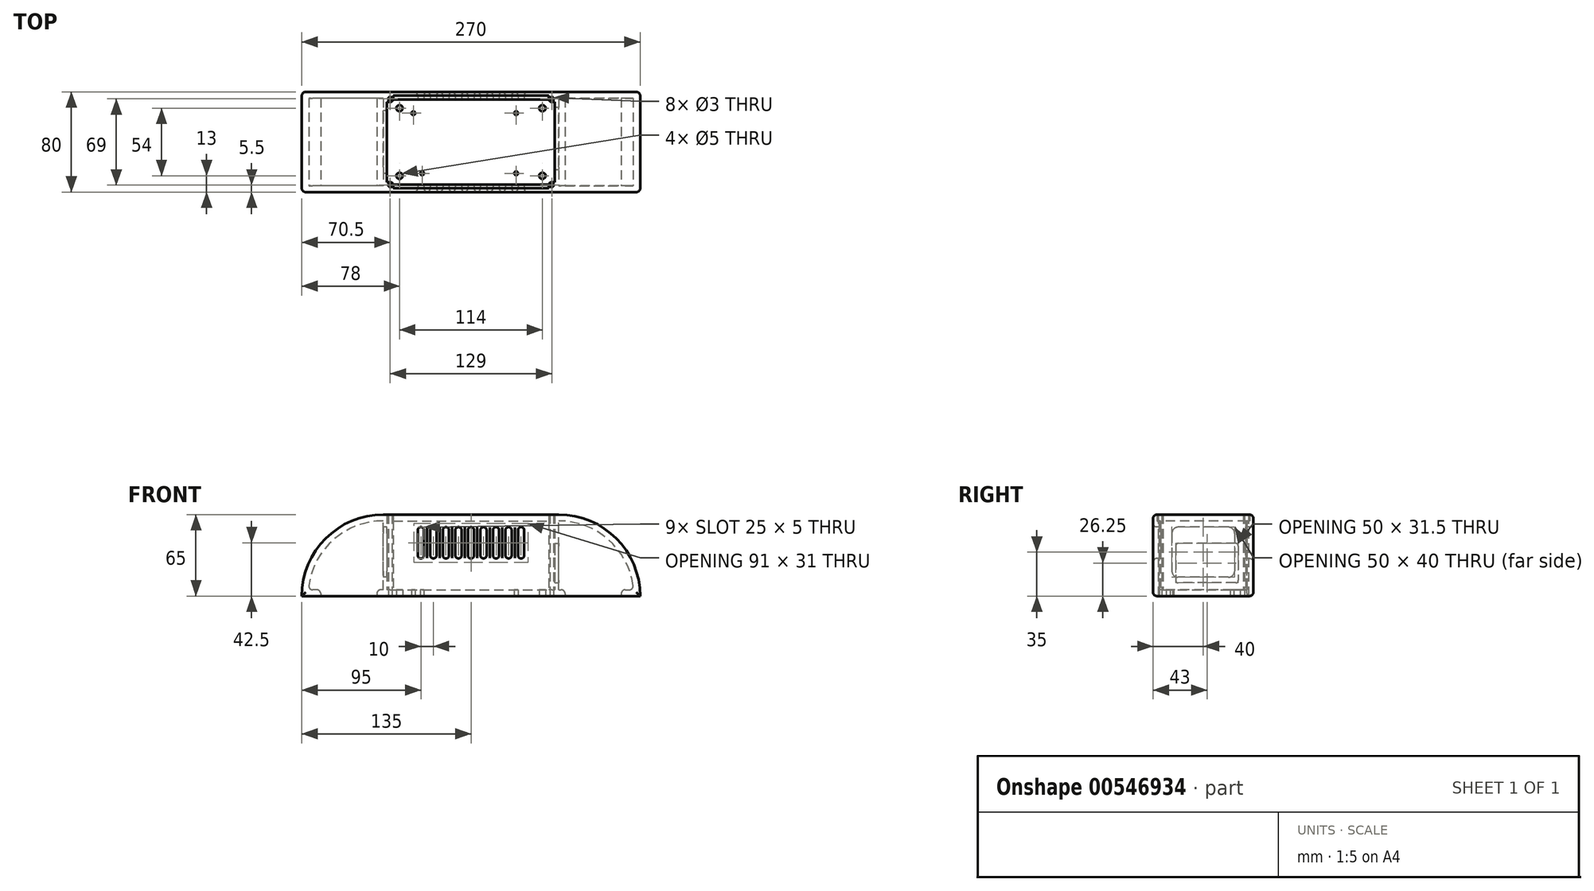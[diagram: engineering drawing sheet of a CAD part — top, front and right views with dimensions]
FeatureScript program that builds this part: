
annotation { "Feature Type Name" : "Feature", "Feature Type Description" : "" }
export const myFeature = defineFeature(function(context is Context, id is Id, definition is map)
    precondition{}
    {
        {
            var Q0;
            Q0=qCreatedBy(makeId("Top.planeOp"),FACE);
            var sketch = newSketch(context, id + "F0", { "sketchPlane" : qUnion([Q0])});
            skLineSegment(sketch, "E0", {"start": v(0, 0) * mm, "end": v(140, 0) * mm});
            skLineSegment(sketch, "E1", {"start": v(140, 0) * mm, "end": v(140, 80) * mm});
            skLineSegment(sketch, "E2", {"start": v(140, 80) * mm, "end": v(0, 80) * mm});
            skLineSegment(sketch, "E3", {"start": v(0, 80) * mm, "end": v(0, 0) * mm});
            skLineSegment(sketch, "E4.0", {"start": v(3, 72) * mm, "end": v(3, 8) * mm});
            skLineSegment(sketch, "E5.0", {"start": v(8, 3) * mm, "end": v(132, 3) * mm});
            skLineSegment(sketch, "E6.0", {"start": v(137, 8) * mm, "end": v(137, 72) * mm});
            skLineSegment(sketch, "E7.0", {"start": v(0, 40) * mm, "end": v(140, 40) * mm, "construction": true});
            skLineSegment(sketch, "E8.0", {"start": v(70, 80) * mm, "end": v(70, 0) * mm, "construction": true});
            skLineSegment(sketch, "E9.0", {"start": v(19, 66) * mm, "end": v(19, 13) * mm, "construction": true});
            skLineSegment(sketch, "E10.0", {"start": v(121, 66) * mm, "end": v(121, 13) * mm, "construction": true});
            skLineSegment(sketch, "E11.0", {"start": v(19, 66) * mm, "end": v(121, 66) * mm, "construction": true});
            skLineSegment(sketch, "E12.0", {"start": v(19, 13) * mm, "end": v(121, 13) * mm, "construction": true});
            skLineSegment(sketch, "E13.0", {"start": v(24, 66) * mm, "end": v(24, 63) * mm, "construction": true});
            skLineSegment(sketch, "E14.0", {"start": v(24, 63) * mm, "end": v(106, 63) * mm, "construction": true});
            skLineSegment(sketch, "E15.0", {"start": v(31, 15) * mm, "end": v(31, 13) * mm, "construction": true});
            skLineSegment(sketch, "E16.0", {"start": v(106, 66) * mm, "end": v(106, 63) * mm, "construction": true});
            skLineSegment(sketch, "E17.0", {"start": v(31, 15) * mm, "end": v(106, 15) * mm, "construction": true});
            skLineSegment(sketch, "E18.trimOffspring", {"start": v(106, 15) * mm, "end": v(106, 13) * mm, "construction": true});
            skCircle(sketch, "E19", {"center": v(24, 63) * mm, "radius": 1.5 * mm});
            skCircle(sketch, "E20", {"center": v(106, 63) * mm, "radius": 1.5 * mm});
            skCircle(sketch, "E21", {"center": v(31, 15) * mm, "radius": 1.5 * mm});
            skCircle(sketch, "E22", {"center": v(106, 15) * mm, "radius": 1.5 * mm});
            skLineSegment(sketch, "E23.0", {"start": v(5.5, 77) * mm, "end": v(5.5, 74.5) * mm, "construction": true});
            skLineSegment(sketch, "E24.0", {"start": v(134.5, 3) * mm, "end": v(134.5, 5.5) * mm, "construction": true});
            skLineSegment(sketch, "E25.0", {"start": v(3, 5.5) * mm, "end": v(5.5, 5.5) * mm, "construction": true});
            skLineSegment(sketch, "E26.0", {"start": v(137, 74.5) * mm, "end": v(134.5, 74.5) * mm, "construction": true});
            skLineSegment(sketch, "E27.trimOffspring", {"start": v(5.5, 74.5) * mm, "end": v(3, 74.5) * mm, "construction": true});
            skLineSegment(sketch, "E28.trimOffspring", {"start": v(134.5, 74.5) * mm, "end": v(134.5, 77) * mm, "construction": true});
            skLineSegment(sketch, "E29.trimOffspring", {"start": v(134.5, 5.5) * mm, "end": v(137, 5.5) * mm, "construction": true});
            skLineSegment(sketch, "E30.trimOffspring", {"start": v(5.5, 5.5) * mm, "end": v(5.5, 3) * mm, "construction": true});
            skLineSegment(sketch, "E31.0", {"start": v(8, 77) * mm, "end": v(8, 74.5) * mm});
            skLineSegment(sketch, "E32.0", {"start": v(132, 3) * mm, "end": v(132, 5.5) * mm});
            skLineSegment(sketch, "E33.0", {"start": v(137, 72) * mm, "end": v(134.5, 72) * mm});
            skLineSegment(sketch, "E34.0", {"start": v(3, 8) * mm, "end": v(5.5, 8) * mm});
            skLineSegment(sketch, "E35.trimOffspring", {"start": v(8, 5.5) * mm, "end": v(8, 3) * mm});
            skLineSegment(sketch, "E36.trimOffspring", {"start": v(5.5, 72) * mm, "end": v(3, 72) * mm});
            skLineSegment(sketch, "E37.trimOffspring", {"start": v(132, 74.5) * mm, "end": v(132, 77) * mm});
            skLineSegment(sketch, "E38.trimOffspring", {"start": v(134.5, 8) * mm, "end": v(137, 8) * mm});
            skPoint(sketch, "E39.visualSharp", {"position": v(8, 72) * mm});
            skArc(sketch, "E39.filletArc", {"start": v(5.5, 72) * mm, "mid": v(7.27, 72.73) * mm, "end": v(8, 74.5) * mm});
            skPoint(sketch, "E40.visualSharp", {"position": v(132, 72) * mm});
            skArc(sketch, "E40.filletArc", {"start": v(132, 74.5) * mm, "mid": v(132.73, 72.73) * mm, "end": v(134.5, 72) * mm});
            skPoint(sketch, "E41.visualSharp", {"position": v(132, 8) * mm});
            skArc(sketch, "E41.filletArc", {"start": v(134.5, 8) * mm, "mid": v(132.73, 7.27) * mm, "end": v(132, 5.5) * mm});
            skPoint(sketch, "E42.visualSharp", {"position": v(8, 8) * mm});
            skArc(sketch, "E42.filletArc", {"start": v(8, 5.5) * mm, "mid": v(7.27, 7.27) * mm, "end": v(5.5, 8) * mm});
            skCircle(sketch, "E43", {"center": v(5.5, 74.5) * mm, "radius": 1.5 * mm});
            skLineSegment(sketch, "E44.trimOffspring", {"start": v(132, 77) * mm, "end": v(8, 77) * mm});
            skCircle(sketch, "E45", {"center": v(134.5, 74.5) * mm, "radius": 1.5 * mm});
            skCircle(sketch, "E46", {"center": v(134.5, 5.5) * mm, "radius": 1.5 * mm});
            skCircle(sketch, "E47", {"center": v(5.5, 5.5) * mm, "radius": 1.5 * mm});
            skLineSegment(sketch, "E48.0", {"start": v(13, 72) * mm, "end": v(13, 8) * mm, "construction": true});
            skLineSegment(sketch, "E49.0", {"start": v(132, 67) * mm, "end": v(127, 67) * mm, "construction": true});
            skLineSegment(sketch, "E50.0", {"start": v(127, 8) * mm, "end": v(127, 72) * mm, "construction": true});
            skLineSegment(sketch, "E51.0", {"start": v(13, 13) * mm, "end": v(127, 13) * mm, "construction": true});
            skLineSegment(sketch, "E52.trimOffspring", {"start": v(13, 67) * mm, "end": v(8, 67) * mm, "construction": true});
            skCircle(sketch, "E53", {"center": v(13, 67) * mm, "radius": 2.5 * mm});
            skCircle(sketch, "E54", {"center": v(127, 67) * mm, "radius": 2.5 * mm});
            skCircle(sketch, "E55", {"center": v(127, 13) * mm, "radius": 2.5 * mm});
            skCircle(sketch, "E56", {"center": v(13, 13) * mm, "radius": 2.5 * mm});
            skLineSegment(sketch, "E57.0", {"start": v(7.95, 6) * mm, "end": v(132.05, 6) * mm});
            skLineSegment(sketch, "E58.0", {"start": v(132.05, 74) * mm, "end": v(7.95, 74) * mm});
            skSolve(sketch);
        }
        {
            var Q0;
            Q0=makeQuery(id+"F0.imprint","IMPRINT",FACE,{"disambiguationData":[TD([[makeQuery(id+"F0.imprint","IMPRINT",EDGE,{"derivedFrom":sQuery(id+"F0.wireOp",EDGE,"E4.0")}),1.0]])]});
            extrude(context, id + "F1", {"entities" : qUnion([Q0]), "depth" : 5 * mm, "offsetDistance" : 25 * mm});
        }
        {
            var Q0;
            Q0=makeQuery(id+"F0.imprint","IMPRINT",FACE,{"disambiguationData":[TD([[makeQuery(id+"F0.imprint","IMPRINT",EDGE,{"derivedFrom":sQuery(id+"F0.wireOp",EDGE,"E0")}),1.0]])]});
            extrude(context, id + "F2", {"entities" : qUnion([Q0]), "operationType" : NewBodyOperationType.ADD, "depth" : 65 * mm, "offsetDistance" : 25 * mm});
        }
        {
            var Q0;
            Q0=qCreatedBy(makeId("Front.planeOp"),FACE);
            var sketch = newSketch(context, id + "F3", { "sketchPlane" : qUnion([Q0])});
            skLineSegment(sketch, "E59", {"start": v(0, 0) * mm, "end": v(0, 30) * mm, "construction": true});
            skLineSegment(sketch, "E60", {"start": v(30, 30) * mm, "end": v(30, 30) * mm});
            skLineSegment(sketch, "E61", {"start": v(0, 30) * mm, "end": v(0, 55) * mm, "construction": true});
            skLineSegment(sketch, "E62", {"start": v(30, 55) * mm, "end": v(30, 55) * mm});
            skLineSegment(sketch, "E63.0", {"start": v(30, 30) * mm, "end": v(30, 55) * mm, "construction": true});
            skLineSegment(sketch, "E64.0", {"start": v(40, 30) * mm, "end": v(40, 55) * mm, "construction": true});
            skLineSegment(sketch, "E65.0", {"start": v(50, 30) * mm, "end": v(50, 55) * mm, "construction": true});
            skLineSegment(sketch, "E66.0", {"start": v(60, 30) * mm, "end": v(60, 55) * mm, "construction": true});
            skLineSegment(sketch, "E67.0", {"start": v(70, 30) * mm, "end": v(70, 55) * mm, "construction": true});
            skLineSegment(sketch, "E68.0", {"start": v(80, 30) * mm, "end": v(80, 55) * mm, "construction": true});
            skLineSegment(sketch, "E69.0", {"start": v(90, 30) * mm, "end": v(90, 55) * mm, "construction": true});
            skLineSegment(sketch, "E70.0", {"start": v(100, 30) * mm, "end": v(100, 55) * mm, "construction": true});
            skLineSegment(sketch, "E71.0", {"start": v(110, 30) * mm, "end": v(110, 55) * mm, "construction": true});
            skLineSegment(sketch, "E72.0", {"start": v(32.5, 32.5) * mm, "end": v(32.5, 52.5) * mm});
            skLineSegment(sketch, "E73.0", {"start": v(27.5, 32.5) * mm, "end": v(27.5, 52.5) * mm});
            skLineSegment(sketch, "E74.MirrorCS", {"start": v(47.5, 32.5) * mm, "end": v(47.5, 52.5) * mm});
            skLineSegment(sketch, "E75.MirrorCS", {"start": v(52.5, 32.5) * mm, "end": v(52.5, 52.5) * mm});
            skLineSegment(sketch, "E76.MirrorCS", {"start": v(67.5, 32.5) * mm, "end": v(67.5, 52.5) * mm});
            skLineSegment(sketch, "E77.MirrorCS", {"start": v(72.5, 32.5) * mm, "end": v(72.5, 52.5) * mm});
            skLineSegment(sketch, "E78.MirrorCS", {"start": v(87.5, 32.5) * mm, "end": v(87.5, 52.5) * mm});
            skLineSegment(sketch, "E79.MirrorCS", {"start": v(92.5, 32.5) * mm, "end": v(92.5, 52.5) * mm});
            skLineSegment(sketch, "E80.MirrorCS", {"start": v(107.5, 32.5) * mm, "end": v(107.5, 52.5) * mm});
            skLineSegment(sketch, "E81.MirrorCS", {"start": v(112.5, 32.5) * mm, "end": v(112.5, 52.5) * mm});
            skLineSegment(sketch, "E82.0", {"start": v(42.5, 32.5) * mm, "end": v(42.5, 52.5) * mm});
            skLineSegment(sketch, "E83.0", {"start": v(37.5, 32.5) * mm, "end": v(37.5, 52.5) * mm});
            skLineSegment(sketch, "E84.MirrorCS", {"start": v(57.5, 32.5) * mm, "end": v(57.5, 52.5) * mm});
            skLineSegment(sketch, "E85.MirrorCS", {"start": v(62.5, 32.5) * mm, "end": v(62.5, 52.5) * mm});
            skLineSegment(sketch, "E86.MirrorCS", {"start": v(77.5, 32.5) * mm, "end": v(77.5, 52.5) * mm});
            skLineSegment(sketch, "E87.MirrorCS", {"start": v(82.5, 32.5) * mm, "end": v(82.5, 52.5) * mm});
            skLineSegment(sketch, "E88.MirrorCS", {"start": v(97.5, 32.5) * mm, "end": v(97.5, 52.5) * mm});
            skLineSegment(sketch, "E89.MirrorCS", {"start": v(102.5, 32.5) * mm, "end": v(102.5, 52.5) * mm});
            skLineSegment(sketch, "E90.trimOffspring", {"start": v(110, 55) * mm, "end": v(110, 55) * mm});
            skLineSegment(sketch, "E91.trimOffspring", {"start": v(100, 55) * mm, "end": v(100, 55) * mm});
            skLineSegment(sketch, "E92.trimOffspring", {"start": v(90, 55) * mm, "end": v(90, 55) * mm});
            skLineSegment(sketch, "E93.trimOffspring", {"start": v(80, 55) * mm, "end": v(80, 55) * mm});
            skLineSegment(sketch, "E94.trimOffspring", {"start": v(70, 55) * mm, "end": v(70, 55) * mm});
            skLineSegment(sketch, "E95.trimOffspring", {"start": v(60, 55) * mm, "end": v(60, 55) * mm});
            skLineSegment(sketch, "E96.trimOffspring", {"start": v(50, 55) * mm, "end": v(50, 55) * mm});
            skLineSegment(sketch, "E97.trimOffspring", {"start": v(40, 55) * mm, "end": v(40, 55) * mm});
            skLineSegment(sketch, "E98.trimOffspring", {"start": v(40, 30) * mm, "end": v(40, 30) * mm});
            skLineSegment(sketch, "E99.trimOffspring", {"start": v(50, 30) * mm, "end": v(50, 30) * mm});
            skLineSegment(sketch, "E100.trimOffspring", {"start": v(60, 30) * mm, "end": v(60, 30) * mm});
            skLineSegment(sketch, "E101.trimOffspring", {"start": v(70, 30) * mm, "end": v(70, 30) * mm});
            skLineSegment(sketch, "E102.trimOffspring", {"start": v(80, 30) * mm, "end": v(80, 30) * mm});
            skLineSegment(sketch, "E103.trimOffspring", {"start": v(90, 30) * mm, "end": v(90, 30) * mm});
            skLineSegment(sketch, "E104.trimOffspring", {"start": v(100, 30) * mm, "end": v(100, 30) * mm});
            skLineSegment(sketch, "E105.trimOffspring", {"start": v(110, 30) * mm, "end": v(110, 30) * mm});
            skPoint(sketch, "E106.visualSharp", {"position": v(27.5, 55) * mm});
            skArc(sketch, "E106.filletArc", {"start": v(30, 55) * mm, "mid": v(28.23, 54.27) * mm, "end": v(27.5, 52.5) * mm});
            skPoint(sketch, "E107.visualSharp", {"position": v(32.5, 55) * mm});
            skArc(sketch, "E107.filletArc", {"start": v(32.5, 52.5) * mm, "mid": v(31.77, 54.27) * mm, "end": v(30, 55) * mm});
            skPoint(sketch, "E108.visualSharp", {"position": v(27.5, 30) * mm});
            skArc(sketch, "E108.filletArc", {"start": v(27.5, 32.5) * mm, "mid": v(28.23, 30.73) * mm, "end": v(30, 30) * mm});
            skPoint(sketch, "E109.visualSharp", {"position": v(32.5, 30) * mm});
            skArc(sketch, "E109.filletArc", {"start": v(30, 30) * mm, "mid": v(31.77, 30.73) * mm, "end": v(32.5, 32.5) * mm});
            skPoint(sketch, "E110.visualSharp", {"position": v(37.5, 30) * mm});
            skArc(sketch, "E110.filletArc", {"start": v(37.5, 32.5) * mm, "mid": v(38.23, 30.73) * mm, "end": v(40, 30) * mm});
            skPoint(sketch, "E111.visualSharp", {"position": v(42.5, 30) * mm});
            skArc(sketch, "E111.filletArc", {"start": v(40, 30) * mm, "mid": v(41.77, 30.73) * mm, "end": v(42.5, 32.5) * mm});
            skPoint(sketch, "E112.visualSharp", {"position": v(37.5, 55) * mm});
            skArc(sketch, "E112.filletArc", {"start": v(40, 55) * mm, "mid": v(38.23, 54.27) * mm, "end": v(37.5, 52.5) * mm});
            skPoint(sketch, "E113.visualSharp", {"position": v(42.5, 55) * mm});
            skArc(sketch, "E113.filletArc", {"start": v(42.5, 52.5) * mm, "mid": v(41.77, 54.27) * mm, "end": v(40, 55) * mm});
            skPoint(sketch, "E114.visualSharp", {"position": v(47.5, 55) * mm});
            skArc(sketch, "E114.filletArc", {"start": v(50, 55) * mm, "mid": v(48.23, 54.27) * mm, "end": v(47.5, 52.5) * mm});
            skPoint(sketch, "E115.visualSharp", {"position": v(52.5, 55) * mm});
            skArc(sketch, "E115.filletArc", {"start": v(52.5, 52.5) * mm, "mid": v(51.77, 54.27) * mm, "end": v(50, 55) * mm});
            skPoint(sketch, "E116.visualSharp", {"position": v(47.5, 30) * mm});
            skArc(sketch, "E116.filletArc", {"start": v(47.5, 32.5) * mm, "mid": v(48.23, 30.73) * mm, "end": v(50, 30) * mm});
            skPoint(sketch, "E117.visualSharp", {"position": v(52.5, 30) * mm});
            skArc(sketch, "E117.filletArc", {"start": v(50, 30) * mm, "mid": v(51.77, 30.73) * mm, "end": v(52.5, 32.5) * mm});
            skPoint(sketch, "E118.visualSharp", {"position": v(57.5, 55) * mm});
            skArc(sketch, "E118.filletArc", {"start": v(60, 55) * mm, "mid": v(58.23, 54.27) * mm, "end": v(57.5, 52.5) * mm});
            skPoint(sketch, "E119.visualSharp", {"position": v(62.5, 55) * mm});
            skArc(sketch, "E119.filletArc", {"start": v(62.5, 52.5) * mm, "mid": v(61.77, 54.27) * mm, "end": v(60, 55) * mm});
            skPoint(sketch, "E120.visualSharp", {"position": v(57.5, 30) * mm});
            skArc(sketch, "E120.filletArc", {"start": v(57.5, 32.5) * mm, "mid": v(58.23, 30.73) * mm, "end": v(60, 30) * mm});
            skPoint(sketch, "E121.visualSharp", {"position": v(62.5, 30) * mm});
            skArc(sketch, "E121.filletArc", {"start": v(60, 30) * mm, "mid": v(61.77, 30.73) * mm, "end": v(62.5, 32.5) * mm});
            skPoint(sketch, "E122.visualSharp", {"position": v(67.5, 55) * mm});
            skArc(sketch, "E122.filletArc", {"start": v(70, 55) * mm, "mid": v(68.23, 54.27) * mm, "end": v(67.5, 52.5) * mm});
            skPoint(sketch, "E123.visualSharp", {"position": v(72.5, 55) * mm});
            skArc(sketch, "E123.filletArc", {"start": v(72.5, 52.5) * mm, "mid": v(71.77, 54.27) * mm, "end": v(70, 55) * mm});
            skPoint(sketch, "E124.visualSharp", {"position": v(67.5, 30) * mm});
            skArc(sketch, "E124.filletArc", {"start": v(67.5, 32.5) * mm, "mid": v(68.23, 30.73) * mm, "end": v(70, 30) * mm});
            skPoint(sketch, "E125.visualSharp", {"position": v(72.5, 30) * mm});
            skArc(sketch, "E125.filletArc", {"start": v(70, 30) * mm, "mid": v(71.77, 30.73) * mm, "end": v(72.5, 32.5) * mm});
            skPoint(sketch, "E126.visualSharp", {"position": v(77.5, 55) * mm});
            skArc(sketch, "E126.filletArc", {"start": v(80, 55) * mm, "mid": v(78.23, 54.27) * mm, "end": v(77.5, 52.5) * mm});
            skPoint(sketch, "E127.visualSharp", {"position": v(82.5, 55) * mm});
            skArc(sketch, "E127.filletArc", {"start": v(82.5, 52.5) * mm, "mid": v(81.77, 54.27) * mm, "end": v(80, 55) * mm});
            skPoint(sketch, "E128.visualSharp", {"position": v(77.5, 30) * mm});
            skArc(sketch, "E128.filletArc", {"start": v(77.5, 32.5) * mm, "mid": v(78.23, 30.73) * mm, "end": v(80, 30) * mm});
            skPoint(sketch, "E129.visualSharp", {"position": v(82.5, 30) * mm});
            skArc(sketch, "E129.filletArc", {"start": v(80, 30) * mm, "mid": v(81.77, 30.73) * mm, "end": v(82.5, 32.5) * mm});
            skPoint(sketch, "E130.visualSharp", {"position": v(87.5, 55) * mm});
            skArc(sketch, "E130.filletArc", {"start": v(90, 55) * mm, "mid": v(88.23, 54.27) * mm, "end": v(87.5, 52.5) * mm});
            skPoint(sketch, "E131.visualSharp", {"position": v(92.5, 55) * mm});
            skArc(sketch, "E131.filletArc", {"start": v(92.5, 52.5) * mm, "mid": v(91.77, 54.27) * mm, "end": v(90, 55) * mm});
            skPoint(sketch, "E132.visualSharp", {"position": v(87.5, 30) * mm});
            skArc(sketch, "E132.filletArc", {"start": v(87.5, 32.5) * mm, "mid": v(88.23, 30.73) * mm, "end": v(90, 30) * mm});
            skPoint(sketch, "E133.visualSharp", {"position": v(92.5, 30) * mm});
            skArc(sketch, "E133.filletArc", {"start": v(90, 30) * mm, "mid": v(91.77, 30.73) * mm, "end": v(92.5, 32.5) * mm});
            skPoint(sketch, "E134.visualSharp", {"position": v(97.5, 55) * mm});
            skArc(sketch, "E134.filletArc", {"start": v(100, 55) * mm, "mid": v(98.23, 54.27) * mm, "end": v(97.5, 52.5) * mm});
            skPoint(sketch, "E135.visualSharp", {"position": v(102.5, 55) * mm});
            skArc(sketch, "E135.filletArc", {"start": v(102.5, 52.5) * mm, "mid": v(101.77, 54.27) * mm, "end": v(100, 55) * mm});
            skPoint(sketch, "E136.visualSharp", {"position": v(97.5, 30) * mm});
            skArc(sketch, "E136.filletArc", {"start": v(97.5, 32.5) * mm, "mid": v(98.23, 30.73) * mm, "end": v(100, 30) * mm});
            skPoint(sketch, "E137.visualSharp", {"position": v(102.5, 30) * mm});
            skArc(sketch, "E137.filletArc", {"start": v(100, 30) * mm, "mid": v(101.77, 30.73) * mm, "end": v(102.5, 32.5) * mm});
            skPoint(sketch, "E138.visualSharp", {"position": v(107.5, 55) * mm});
            skArc(sketch, "E138.filletArc", {"start": v(110, 55) * mm, "mid": v(108.23, 54.27) * mm, "end": v(107.5, 52.5) * mm});
            skPoint(sketch, "E139.visualSharp", {"position": v(112.5, 55) * mm});
            skArc(sketch, "E139.filletArc", {"start": v(112.5, 52.5) * mm, "mid": v(111.77, 54.27) * mm, "end": v(110, 55) * mm});
            skPoint(sketch, "E140.visualSharp", {"position": v(107.5, 30) * mm});
            skArc(sketch, "E140.filletArc", {"start": v(107.5, 32.5) * mm, "mid": v(108.23, 30.73) * mm, "end": v(110, 30) * mm});
            skPoint(sketch, "E141.visualSharp", {"position": v(112.5, 30) * mm});
            skArc(sketch, "E141.filletArc", {"start": v(110, 30) * mm, "mid": v(111.77, 30.73) * mm, "end": v(112.5, 32.5) * mm});
            skArc(sketch, "E142", {"start": v(0, 65) * mm, "mid": v(-45.96, 45.96) * mm, "end": v(-65, 0) * mm});
            skLineSegment(sketch, "E143", {"start": v(0, 0) * mm, "end": v(0, 65) * mm});
            skLineSegment(sketch, "E144", {"start": v(0, 0) * mm, "end": v(-65, 0) * mm});
            skLineSegment(sketch, "E145", {"start": v(0, 0) * mm, "end": v(140, 0) * mm, "construction": true});
            skLineSegment(sketch, "E146", {"start": v(140, 0) * mm, "end": v(140, 65) * mm});
            skLineSegment(sketch, "E147", {"start": v(140, 0) * mm, "end": v(205, 0) * mm});
            skArc(sketch, "E148", {"start": v(205, 0) * mm, "mid": v(185.96, 45.96) * mm, "end": v(140, 65) * mm});
            skSolve(sketch);
        }
        {
            var Q0;
            Q0=qCreatedBy(makeId("Right.planeOp"),FACE);
            var sketch = newSketch(context, id + "F4", { "sketchPlane" : qUnion([Q0])});
            skLineSegment(sketch, "E149", {"start": v(0, 0) * mm, "end": v(0, 55) * mm, "construction": true});
            skLineSegment(sketch, "E150", {"start": v(20, 55) * mm, "end": v(60, 55) * mm});
            skLineSegment(sketch, "E151.0", {"start": v(40, 0) * mm, "end": v(40, 55) * mm, "construction": true});
            skLineSegment(sketch, "E152.0", {"start": v(35, 45) * mm, "end": v(35, 55) * mm, "construction": true});
            skLineSegment(sketch, "E153.0", {"start": v(65, 20) * mm, "end": v(65, 50) * mm});
            skLineSegment(sketch, "E154.0", {"start": v(15, 20) * mm, "end": v(15, 50) * mm});
            skLineSegment(sketch, "E155.0", {"start": v(20, 15) * mm, "end": v(60, 15) * mm});
            skPoint(sketch, "E156.visualSharp", {"position": v(65, 55) * mm});
            skArc(sketch, "E156.filletArc", {"start": v(65, 50) * mm, "mid": v(63.54, 53.54) * mm, "end": v(60, 55) * mm});
            skPoint(sketch, "E157.visualSharp", {"position": v(15, 55) * mm});
            skArc(sketch, "E157.filletArc", {"start": v(20, 55) * mm, "mid": v(16.46, 53.54) * mm, "end": v(15, 50) * mm});
            skPoint(sketch, "E158.visualSharp", {"position": v(15, 15) * mm});
            skArc(sketch, "E158.filletArc", {"start": v(15, 20) * mm, "mid": v(16.46, 16.46) * mm, "end": v(20, 15) * mm});
            skPoint(sketch, "E159.visualSharp", {"position": v(65, 15) * mm});
            skArc(sketch, "E159.filletArc", {"start": v(60, 15) * mm, "mid": v(63.54, 16.46) * mm, "end": v(65, 20) * mm});
            skSolve(sketch);
        }
        {
            var Q0;
            Q0=makeQuery(id+"F4.imprint","IMPRINT",FACE,{"disambiguationData":[TD([[makeQuery(id+"F4.imprint","IMPRINT",EDGE,{"derivedFrom":sQuery(id+"F4.wireOp",EDGE,"E150")}),-1.0]])]});
            extrude(context, id + "F5", {"entities" : qUnion([Q0]), "operationType" : NewBodyOperationType.REMOVE, "depth" : 10 * mm, "offsetDistance" : 25 * mm});
        }
        {
            var Q0;
            Q0=qCreatedBy(makeId("Right.planeOp"),FACE);
            cPlane(context, id + "F6", {"entities" : qUnion([Q0]), "cplaneType" : CPlaneType.OFFSET, "offset" : 140 * mm, "width" : 150 * mm, "height" : 150 * mm});
        }
        {
            var Q0;
            Q0=qCreatedBy(id+"F6.planeOp",FACE);
            var sketch = newSketch(context, id + "F7", { "sketchPlane" : qUnion([Q0])});
            skLineSegment(sketch, "E160", {"start": v(0, 0) * mm, "end": v(0, 65) * mm, "construction": true});
            skLineSegment(sketch, "E161.0", {"start": v(40, 0) * mm, "end": v(40, 65) * mm, "construction": true});
            skLineSegment(sketch, "E162.0", {"start": v(68, 12.5) * mm, "end": v(68, 40) * mm});
            skLineSegment(sketch, "E163.0", {"start": v(18, 12.5) * mm, "end": v(18, 40) * mm});
            skLineSegment(sketch, "E164.0", {"start": v(20, 10.5) * mm, "end": v(66, 10.5) * mm});
            skLineSegment(sketch, "E165.0", {"start": v(20, 42) * mm, "end": v(66, 42) * mm});
            skPoint(sketch, "E166.visualSharp", {"position": v(68, 42) * mm});
            skArc(sketch, "E166.filletArc", {"start": v(68, 40) * mm, "mid": v(67.41, 41.41) * mm, "end": v(66, 42) * mm});
            skPoint(sketch, "E167.visualSharp", {"position": v(18, 42) * mm});
            skArc(sketch, "E167.filletArc", {"start": v(20, 42) * mm, "mid": v(18.59, 41.41) * mm, "end": v(18, 40) * mm});
            skPoint(sketch, "E168.visualSharp", {"position": v(18, 10.5) * mm});
            skArc(sketch, "E168.filletArc", {"start": v(18, 12.5) * mm, "mid": v(18.59, 11.09) * mm, "end": v(20, 10.5) * mm});
            skPoint(sketch, "E169.visualSharp", {"position": v(68, 10.5) * mm});
            skArc(sketch, "E169.filletArc", {"start": v(66, 10.5) * mm, "mid": v(67.41, 11.09) * mm, "end": v(68, 12.5) * mm});
            skSolve(sketch);
        }
        {
            var Q0;
            Q0=makeQuery(id+"F7.imprint","IMPRINT",FACE,{"disambiguationData":[TD([[makeQuery(id+"F7.imprint","IMPRINT",EDGE,{"derivedFrom":sQuery(id+"F7.wireOp",EDGE,"E163.0")}),-1.0]])]});
            var Q1;
            Q1=makeQuery(id+"F7.imprint","IMPRINT",FACE,{"disambiguationData":[TD([[makeQuery(id+"F7.imprint","IMPRINT",EDGE,{"derivedFrom":sQuery(id+"F7.wireOp",EDGE,"E162.0")}),1.0]])]});
            extrude(context, id + "F8", {"entities" : qUnion([Q0, Q1]), "operationType" : NewBodyOperationType.REMOVE, "oppositeDirection" : true, "depth" : 10 * mm, "offsetDistance" : 25 * mm});
        }
        {
            var Q0;
            Q0=makeQuery(id+"F0.imprint","IMPRINT",FACE,{"disambiguationData":[TD([[makeQuery(id+"F0.imprint","IMPRINT",EDGE,{"derivedFrom":sQuery(id+"F0.wireOp",EDGE,"E5.0")}),1.0]])]});
            var Q1;
            {var subQ1=sQuery(id+"F0.wireOp",EDGE,"E31.0");Q1=makeQuery(id+"F0.imprint","IMPRINT",FACE,{"disambiguationData":[TD([[makeQuery(id+"F0.imprint","IMPRINT",EDGE,{"derivedFrom":subQ1}),1.0]])]});}
            extrude(context, id + "F9", {"entities" : qUnion([Q0, Q1]), "operationType" : NewBodyOperationType.ADD, "depth" : 60 * mm, "offsetDistance" : 25 * mm});
        }
        {
            var Q0;
            Q0=makeQuery(id+"F3.imprint","IMPRINT",FACE,{"disambiguationData":[TD([[makeQuery(id+"F3.imprint","IMPRINT",EDGE,{"derivedFrom":sQuery(id+"F3.wireOp",EDGE,"E72.0")}),1.0]])]});
            var Q1;
            Q1=makeQuery(id+"F3.imprint","IMPRINT",FACE,{"disambiguationData":[TD([[makeQuery(id+"F3.imprint","IMPRINT",EDGE,{"derivedFrom":sQuery(id+"F3.wireOp",EDGE,"E82.0")}),1.0]])]});
            var Q2;
            Q2=makeQuery(id+"F3.imprint","IMPRINT",FACE,{"disambiguationData":[TD([[makeQuery(id+"F3.imprint","IMPRINT",EDGE,{"derivedFrom":sQuery(id+"F3.wireOp",EDGE,"E74.MirrorCS")}),-1.0]])]});
            var Q3;
            Q3=makeQuery(id+"F3.imprint","IMPRINT",FACE,{"disambiguationData":[TD([[makeQuery(id+"F3.imprint","IMPRINT",EDGE,{"derivedFrom":sQuery(id+"F3.wireOp",EDGE,"E84.MirrorCS")}),-1.0]])]});
            var Q4;
            Q4=makeQuery(id+"F3.imprint","IMPRINT",FACE,{"disambiguationData":[TD([[makeQuery(id+"F3.imprint","IMPRINT",EDGE,{"derivedFrom":sQuery(id+"F3.wireOp",EDGE,"E76.MirrorCS")}),-1.0]])]});
            var Q5;
            Q5=makeQuery(id+"F3.imprint","IMPRINT",FACE,{"disambiguationData":[TD([[makeQuery(id+"F3.imprint","IMPRINT",EDGE,{"derivedFrom":sQuery(id+"F3.wireOp",EDGE,"E86.MirrorCS")}),-1.0]])]});
            var Q6;
            Q6=makeQuery(id+"F3.imprint","IMPRINT",FACE,{"disambiguationData":[TD([[makeQuery(id+"F3.imprint","IMPRINT",EDGE,{"derivedFrom":sQuery(id+"F3.wireOp",EDGE,"E78.MirrorCS")}),-1.0]])]});
            var Q7;
            Q7=makeQuery(id+"F3.imprint","IMPRINT",FACE,{"disambiguationData":[TD([[makeQuery(id+"F3.imprint","IMPRINT",EDGE,{"derivedFrom":sQuery(id+"F3.wireOp",EDGE,"E88.MirrorCS")}),-1.0]])]});
            var Q8;
            Q8=makeQuery(id+"F3.imprint","IMPRINT",FACE,{"disambiguationData":[TD([[makeQuery(id+"F3.imprint","IMPRINT",EDGE,{"derivedFrom":sQuery(id+"F3.wireOp",EDGE,"E80.MirrorCS")}),-1.0]])]});
            extrude(context, id + "F10", {"entities" : qUnion([Q0, Q1, Q2, Q3, Q4, Q5, Q6, Q7, Q8]), "operationType" : NewBodyOperationType.REMOVE, "oppositeDirection" : true, "depth" : 85 * mm, "offsetDistance" : 25 * mm});
        }
        {
            var Q0;
            Q0=qCreatedBy(makeId("Front.planeOp"),FACE);
            cPlane(context, id + "F11", {"entities" : qUnion([Q0]), "cplaneType" : CPlaneType.OFFSET, "offset" : 5 * mm, "oppositeDirection" : true, "width" : 150 * mm, "height" : 150 * mm});
        }
        {
            var Q0;
            Q0=qCreatedBy(id+"F11.planeOp",FACE);
            var sketch = newSketch(context, id + "F12", { "sketchPlane" : qUnion([Q0])});
            skLineSegment(sketch, "E170", {"start": v(0, 0) * mm, "end": v(140, 0) * mm, "construction": true});
            skLineSegment(sketch, "E171", {"start": v(140, 0) * mm, "end": v(140, 5) * mm});
            skLineSegment(sketch, "E172", {"start": v(140, 5) * mm, "end": v(145, 5) * mm});
            skLineSegment(sketch, "E173", {"start": v(145, 5) * mm, "end": v(145, 0) * mm});
            skLineSegment(sketch, "E174", {"start": v(145, 0) * mm, "end": v(190, 0) * mm});
            skArc(sketch, "E175", {"start": v(199.8, 5) * mm, "mid": v(180.62, 44.16) * mm, "end": v(140, 60) * mm});
            skLineSegment(sketch, "E176", {"start": v(140, 5) * mm, "end": v(140, 60) * mm});
            skPoint(sketch, "E177.orphan", {"position": v(140, 50) * mm});
            skLineSegment(sketch, "E178.0", {"start": v(190, 5) * mm, "end": v(199.8, 5) * mm});
            skLineSegment(sketch, "E179.0", {"start": v(190, 5) * mm, "end": v(190, 0) * mm});
            skLineSegment(sketch, "E180", {"start": v(0, 0) * mm, "end": v(0, 5) * mm});
            skLineSegment(sketch, "E181", {"start": v(0, 5) * mm, "end": v(-5, 5) * mm});
            skLineSegment(sketch, "E182", {"start": v(-5, 5) * mm, "end": v(-5, 0) * mm});
            skLineSegment(sketch, "E183", {"start": v(-5, 0) * mm, "end": v(-50, 0) * mm});
            skLineSegment(sketch, "E184", {"start": v(0, 5) * mm, "end": v(0, 60) * mm});
            skArc(sketch, "E185", {"start": v(0, 60) * mm, "mid": v(-40.62, 44.16) * mm, "end": v(-59.8, 5) * mm});
            skLineSegment(sketch, "E186.0", {"start": v(-50, 5) * mm, "end": v(-59.8, 5) * mm});
            skLineSegment(sketch, "E187.0", {"start": v(-50, 5) * mm, "end": v(-50, 0) * mm});
            skSolve(sketch);
        }
        {
            var Q0;
            Q0=makeQuery(id+"F3.imprint","IMPRINT",FACE,{"disambiguationData":[TD([[makeQuery(id+"F3.imprint","IMPRINT",EDGE,{"derivedFrom":sQuery(id+"F3.wireOp",EDGE,"E146")}),-1.0]])]});
            var Q1;
            Q1=makeQuery(id+"F3.imprint","IMPRINT",FACE,{"disambiguationData":[TD([[makeQuery(id+"F3.imprint","IMPRINT",EDGE,{"derivedFrom":sQuery(id+"F3.wireOp",EDGE,"E142")}),1.0]])]});
            extrude(context, id + "F13", {"entities" : qUnion([Q0, Q1]), "operationType" : NewBodyOperationType.ADD, "oppositeDirection" : true, "depth" : 80 * mm, "offsetDistance" : 25 * mm});
        }
        {
            var Q0;
            Q0 = qSketchRegion(id + "F12", true);
            extrude(context, id + "F14", {"entities" : qUnion([Q0]), "operationType" : NewBodyOperationType.REMOVE, "oppositeDirection" : true, "depth" : 70 * mm, "offsetDistance" : 25 * mm});
        }
        {
            var Q0;
            Q0=makeQuery(id+"F13.opExtrude","CAP_EDGE",EDGE,{"disambiguationData":[OSD([sQuery(id+"F3.wireOp",EDGE,"E142")])],"isStart":true});
            var Q1;
            Q1=makeQuery(id+"F13.opExtrude","CAP_EDGE",EDGE,{"disambiguationData":[OSD([sQuery(id+"F3.wireOp",EDGE,"E142")])],"isStart":false});
            var Q2;
            Q2=makeQuery(id+"F13.boolean.opBoolean","MERGE",FACE,{"derivedFrom":[makeQuery(id+"F2.opExtrude","SWEPT_FACE",FACE,{"disambiguationData":[OSD([sQuery(id+"F0.wireOp",EDGE,"E2")])]}),makeQuery(id+"F13.opExtrude","CAP_FACE",FACE,{"disambiguationData":[OSD([sQuery(id+"F3.wireOp",EDGE,"E142"),sQuery(id+"F3.wireOp",EDGE,"E143"),sQuery(id+"F3.wireOp",EDGE,"E144")])],"isStart":false}),makeQuery(id+"F13.opExtrude","CAP_FACE",FACE,{"disambiguationData":[OSD([sQuery(id+"F3.wireOp",EDGE,"E146"),sQuery(id+"F3.wireOp",EDGE,"E147"),sQuery(id+"F3.wireOp",EDGE,"E148")])],"isStart":false})]});
            var Q3;
            Q3=makeQuery(id+"F13.boolean.opBoolean","MERGE",FACE,{"derivedFrom":[makeQuery(id+"F2.opExtrude","SWEPT_FACE",FACE,{"disambiguationData":[OSD([sQuery(id+"F0.wireOp",EDGE,"E0")])]}),makeQuery(id+"F13.opExtrude","CAP_FACE",FACE,{"disambiguationData":[OSD([sQuery(id+"F3.wireOp",EDGE,"E142"),sQuery(id+"F3.wireOp",EDGE,"E143"),sQuery(id+"F3.wireOp",EDGE,"E144")])],"isStart":true}),makeQuery(id+"F13.opExtrude","CAP_FACE",FACE,{"disambiguationData":[OSD([sQuery(id+"F3.wireOp",EDGE,"E146"),sQuery(id+"F3.wireOp",EDGE,"E147"),sQuery(id+"F3.wireOp",EDGE,"E148")])],"isStart":true})]});
            var Q4;
            Q4=makeQuery(id+"F14.boolean.opBoolean","COPY",EDGE,{"derivedFrom":makeQuery(id+"F14.opExtrude","SWEPT_EDGE",EDGE,{"disambiguationData":[OSD([sQuery(id+"F12.wireOp",EDGE,"E178.0"),sQuery(id+"F12.wireOp",EDGE,"E179.0")])]})});
            var Q5;
            Q5=makeQuery(id+"F14.boolean.opBoolean","COPY",EDGE,{"derivedFrom":makeQuery(id+"F14.opExtrude","SWEPT_EDGE",EDGE,{"disambiguationData":[OSD([sQuery(id+"F12.wireOp",EDGE,"E175"),sQuery(id+"F12.wireOp",EDGE,"E178.0")])]})});
            var Q6;
            Q6=makeQuery(id+"F14.boolean.opBoolean","COPY",EDGE,{"derivedFrom":makeQuery(id+"F14.opExtrude","SWEPT_EDGE",EDGE,{"disambiguationData":[OSD([sQuery(id+"F12.wireOp",EDGE,"E186.0"),sQuery(id+"F12.wireOp",EDGE,"E187.0")])]})});
            var Q7;
            Q7=makeQuery(id+"F14.boolean.opBoolean","COPY",EDGE,{"derivedFrom":makeQuery(id+"F14.opExtrude","SWEPT_EDGE",EDGE,{"disambiguationData":[OSD([sQuery(id+"F12.wireOp",EDGE,"E185"),sQuery(id+"F12.wireOp",EDGE,"E186.0")])]})});
            var Q8;
            Q8=makeQuery(id+"F14.boolean.opBoolean","COPY",EDGE,{"derivedFrom":makeQuery(id+"F14.opExtrude","SWEPT_EDGE",EDGE,{"disambiguationData":[OSD([sQuery(id+"F12.wireOp",EDGE,"E172"),sQuery(id+"F12.wireOp",EDGE,"E173")])]})});
            var Q9;
            Q9=makeQuery(id+"F8.boolean.opBoolean","COPY",EDGE,{"derivedFrom":makeQuery(id+"F8.opExtrude","CAP_EDGE",EDGE,{"disambiguationData":[OSD([sQuery(id+"F7.wireOp",EDGE,"E164.0")])],"isStart":true})});
            var Q10;
            Q10=makeQuery(id+"F14.boolean.opBoolean","COPY",EDGE,{"derivedFrom":makeQuery(id+"F14.opExtrude","SWEPT_EDGE",EDGE,{"disambiguationData":[OSD([sQuery(id+"F12.wireOp",EDGE,"E181"),sQuery(id+"F12.wireOp",EDGE,"E182")])]})});
            var Q11;
            Q11=makeQuery(id+"F5.boolean.opBoolean","COPY",EDGE,{"derivedFrom":makeQuery(id+"F5.opExtrude","CAP_EDGE",EDGE,{"disambiguationData":[OSD([sQuery(id+"F4.wireOp",EDGE,"E155.0")])],"isStart":true})});
            fillet(context, id + "F15", {"entities" : qUnion([Q0, Q1, Q2, Q3, Q4, Q5, Q6, Q7, Q8, Q9, Q10, Q11]), "radius" : 3 * mm, "tangentPropagation" : true, "allowEdgeOverflow" : false});
        }
    });
